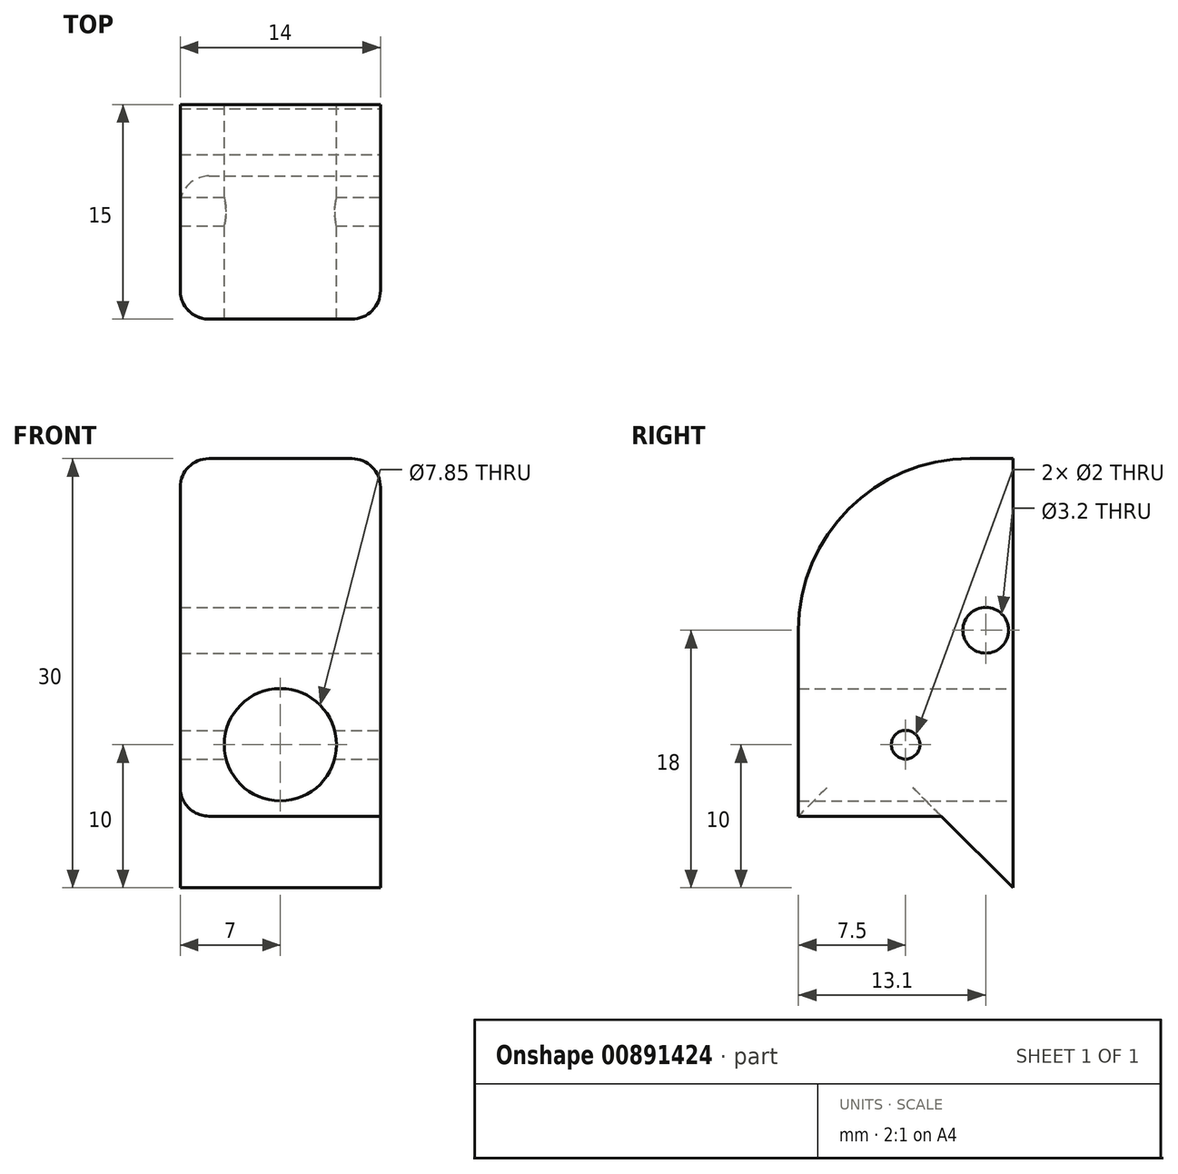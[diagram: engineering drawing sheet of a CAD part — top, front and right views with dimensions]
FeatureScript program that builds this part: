
annotation { "Feature Type Name" : "Feature", "Feature Type Description" : "" }
export const myFeature = defineFeature(function(context is Context, id is Id, definition is map)
    precondition{}
    {
        {
            var Q0;
            Q0=qCreatedBy(makeId("Front.planeOp"),FACE);
            var sketch = newSketch(context, id + "F0", { "sketchPlane" : qUnion([Q0])});
            skCircle(sketch, "E0", {"center": v(0, 0) * mm, "radius": 3.92 * mm});
            skLineSegment(sketch, "E1.bottom", {"start": v(-7, 20) * mm, "end": v(7, 20) * mm});
            skLineSegment(sketch, "E1.top", {"start": v(-7, -10) * mm, "end": v(7, -10) * mm});
            skLineSegment(sketch, "E1.left", {"start": v(-7, 20) * mm, "end": v(-7, -10) * mm});
            skLineSegment(sketch, "E1.right", {"start": v(7, 20) * mm, "end": v(7, -10) * mm});
            skSolve(sketch);
        }
        {
            var Q0;
            Q0 = qSketchRegion(id + "F0", true);
            extrude(context, id + "F1", {"entities" : qUnion([Q0]), "depth" : 15 * mm, "offsetDistance" : 25 * mm});
        }
        {
            var Q0;
            Q0=makeQuery(id+"F1.opExtrude","SWEPT_FACE",FACE,{"disambiguationData":[OSD([sQuery(id+"F0.wireOp",EDGE,"E1.right")])]});
            var sketch = newSketch(context, id + "F2", { "sketchPlane" : qUnion([Q0])});
            skLineSegment(sketch, "E2", {"start": v(0, -10) * mm, "end": v(-5, -5) * mm});
            skLineSegment(sketch, "E3", {"start": v(-5, -5) * mm, "end": v(-15, -5) * mm});
            skLineSegment(sketch, "E4", {"start": v(-15, -5) * mm, "end": v(-15, -10) * mm});
            skLineSegment(sketch, "E5", {"start": v(-15, -10) * mm, "end": v(0, -10) * mm});
            skSolve(sketch);
        }
        {
            var Q0;
            Q0 = qSketchRegion(id + "F2", true);
            extrude(context, id + "F3", {"entities" : qUnion([Q0]), "operationType" : NewBodyOperationType.REMOVE, "endBound" : BoundingType.THROUGH_ALL, "oppositeDirection" : true, "depth" : 25 * mm, "offsetDistance" : 25 * mm});
        }
        {
            var Q0;
            Q0=makeQuery(id+"F1.opExtrude","SWEPT_FACE",FACE,{"disambiguationData":[OSD([sQuery(id+"F0.wireOp",EDGE,"E1.right")])]});
            var sketch = newSketch(context, id + "F4", { "sketchPlane" : qUnion([Q0])});
            skCircle(sketch, "E6", {"center": v(-1.9, 8) * mm, "radius": 1.6 * mm});
            skCircle(sketch, "E7", {"center": v(-7.5, 0) * mm, "radius": 1 * mm});
            skSolve(sketch);
        }
        {
            var Q0;
            Q0 = qSketchRegion(id + "F4", true);
            extrude(context, id + "F5", {"entities" : qUnion([Q0]), "operationType" : NewBodyOperationType.REMOVE, "endBound" : BoundingType.THROUGH_ALL, "oppositeDirection" : true, "depth" : 25 * mm, "offsetDistance" : 25 * mm});
        }
        {
            var Q0;
            Q0=makeQuery(id+"F1.opExtrude","CAP_EDGE",EDGE,{"disambiguationData":[OSD([sQuery(id+"F0.wireOp",EDGE,"E1.bottom")])],"isStart":false});
            fillet(context, id + "F6", {"entities" : qUnion([Q0]), "radius" : 12 * mm, "tangentPropagation" : true, "allowEdgeOverflow" : false});
        }
        {
            var Q0;
            Q0=makeQuery(id+"F3.boolean.opBoolean","COPY",EDGE,{"derivedFrom":makeQuery(id+"F3.opExtrude","SWEPT_EDGE",EDGE,{"disambiguationData":[OSD([sQuery(id+"F0.wireOp",EDGE,"E1.right"),sQuery(id+"F2.wireOp",EDGE,"E3"),sQuery(id+"F2.wireOp",EDGE,"E4")])]})});
            var Q1;
            Q1=makeQuery(id+"F1.opExtrude","CAP_EDGE",EDGE,{"disambiguationData":[OSD([sQuery(id+"F0.wireOp",EDGE,"E1.right")])],"isStart":false});
            var Q2;
            Q2=makeQuery(id+"F3.boolean.opBoolean","INTERSECT",EDGE,{"derivedFrom":[makeQuery(id+"F1.opExtrude","SWEPT_FACE",FACE,{"disambiguationData":[OSD([sQuery(id+"F0.wireOp",EDGE,"E1.left")])]}),makeQuery(id+"F3.opExtrude","SWEPT_FACE",FACE,{"disambiguationData":[OSD([sQuery(id+"F2.wireOp",EDGE,"E3")])]})]});
            var Q3;
            Q3=makeQuery(id+"F1.opExtrude","CAP_EDGE",EDGE,{"disambiguationData":[OSD([sQuery(id+"F0.wireOp",EDGE,"E1.left")])],"isStart":false});
            var Q4;
            Q4=makeQuery(id+"F6.opFillet","BLEND_EDGE",EDGE,{"blendedFrom":[makeQuery(id+"F1.opExtrude","CAP_EDGE",EDGE,{"disambiguationData":[OSD([sQuery(id+"F0.wireOp",EDGE,"E1.bottom")])],"isStart":false}),makeQuery(id+"F1.opExtrude","SWEPT_FACE",FACE,{"disambiguationData":[OSD([sQuery(id+"F0.wireOp",EDGE,"E1.left")])]})],"blendedInto":[makeQuery(id+"F1.opExtrude","SWEPT_FACE",FACE,{"disambiguationData":[OSD([sQuery(id+"F0.wireOp",EDGE,"E1.left")])]})]});
            var Q5;
            Q5=makeQuery(id+"F3.boolean.opBoolean","COPY",EDGE,{"derivedFrom":makeQuery(id+"F3.opExtrude","CAP_EDGE",EDGE,{"disambiguationData":[OSD([sQuery(id+"F2.wireOp",EDGE,"E3")])],"isStart":true})});
            fillet(context, id + "F7", {"entities" : qUnion([Q0, Q1, Q2, Q3, Q4, Q5]), "radius" : 2 * mm, "tangentPropagation" : true, "allowEdgeOverflow" : false});
        }
    });
